# Revit family: Furniture_Other_Sjobergs_Duplex_2-station
name_source: partatom
category: Furniture
revit_build: Autodesk Revit 2018 (Build: 20170223_1515(x64)
units: mm (PartAtom-declared; Revit-internal decimal feet)

## family parameters
Always vertical = Yes
Cut with Voids When Loaded = No
OmniClass Number = 23.40.70.14
OmniClass Title = Retail and Commercial Equipment and Furnishings
Room Calculation Point = No
Shared = No
Work Plane-Based = No

## types (1)
- Duplex, 2-station
    AssetType = Movable
    BIMObjectName = Furniture_Other_Sjobergs_Duplex_2-station
    Brand = Sjöbergs
    Category = Workbench
    Collection = Duplex
    Color = Wooden
    Cost = 0 $
    Description = SJÖBERGS DUPLEX is the perfect 2-station. It can be used by two right-handed, two left-handed, or one right- and one left-handed.
The massive lacquered beech top is 60 mm thick and includes a heavily constructed vise, making it an exceptionally flexible and sturdy workstation.
The gas springs are replacable with hydraulic raising. Adjustable in height between 700-900 mm.
    DurationUnit = Year
    Features = The massive lacquered beech top is 60 mm thick and includes a heavily constructed vise, making it an exceptionally flexible and sturdy workstation.
The gas springs are replacable with hydraulic raising. Adjustable in height between 700-900 mm.
    Finish = Lacquered beech.
    IfcExportAs = IfcFurnishingElementType
    IfcExportType = TABLE
    MainColor = Wooden
    Manufacturer = Sjöbergs
    ManufacturerName = Sjöbergs
    ManufacturerURL = https://www.sjobergs.se
    Material = Wood, metal
    Model = Duplex, 2-station
    ModelReference = 33083
    NBSDescription = School art, design and technology tables and workbenches;
    NBSReference = 45-35-20/320
    Name = Duplex_2-station
    NominalDepth = 870 mm
    Nominal_Height = 900 mm  [stored 2.95276 ft]
    Nominal_Width = 1335 mm
    ProductDatasheet = https://sjobergs.se
    ProductInformation = SJÖBERGS DUPLEX is the perfect 2-station. It can be used by two right-handed, two left-handed, or one right- and one left-handed.
The massive lacquered beech top is 60 mm thick and includes a heavily constructed vise, making it an exceptionally flexible and sturdy workstation.
The gas springs are replacable with hydraulic raising. Adjustable in height between 700-900 mm.
    Shape = Sculptured
    Size = 1200x870x900 mm
    TableMainMaterial = Beech
    TableSecondaryMaterial = Stainless Steel
    TableTertiaryMaterial = Plastic, Opaque Black
    URL = https://sjobergs.se
    Uniclass2 = Pr_40_50_21
    Uniclass2015Description = Desks, Tables And Worktops
    Uniclass2015Reference = Pr_40_50_21_76
    Version = 1
    VersionDate = 01/04/2022
    WarrantyDurationUnit = Year
    Weight = 83.3 Kg

note: [stored X ft] marks values corroborated as IEEE doubles in the binary element streams (Revit-internal decimal feet)

## geometry (parser evidence)
native form markers: Sweep x5
no freeform markers — native parametric forms only
